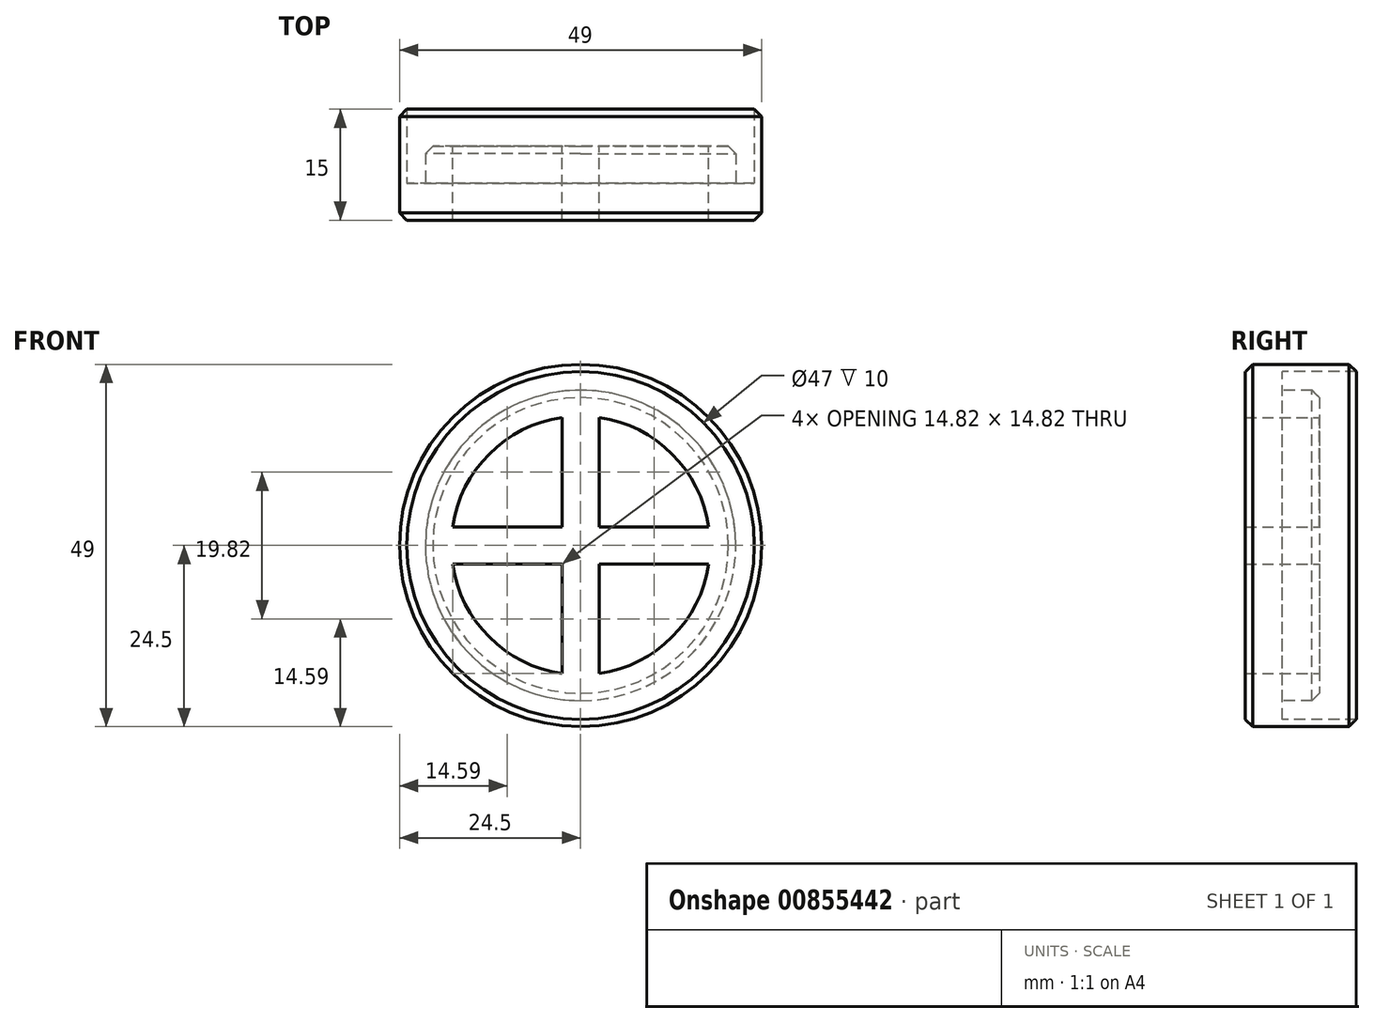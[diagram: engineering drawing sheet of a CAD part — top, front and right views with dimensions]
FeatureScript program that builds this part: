
annotation { "Feature Type Name" : "Feature", "Feature Type Description" : "" }
export const myFeature = defineFeature(function(context is Context, id is Id, definition is map)
    precondition{}
    {
        {
            var Q0;
            Q0=qCreatedBy(makeId("Top.planeOp"),FACE);
            var sketch = newSketch(context, id + "F0", { "sketchPlane" : qUnion([Q0])});
            skLineSegment(sketch, "E0", {"start": v(-24.5, 0) * mm, "end": v(0, 0) * mm});
            skLineSegment(sketch, "E1", {"start": v(-21, 10) * mm, "end": v(0, 10) * mm});
            skLineSegment(sketch, "E2", {"start": v(-24.5, 0) * mm, "end": v(-24.5, 15) * mm});
            skLineSegment(sketch, "E3", {"start": v(-24.5, 15) * mm, "end": v(-23.5, 15) * mm});
            skLineSegment(sketch, "E4", {"start": v(-23.5, 15) * mm, "end": v(-23.5, 5) * mm});
            skLineSegment(sketch, "E5", {"start": v(-23.5, 5) * mm, "end": v(-21, 5) * mm});
            skLineSegment(sketch, "E6", {"start": v(-21, 5) * mm, "end": v(-21, 10) * mm});
            skLineSegment(sketch, "E7", {"start": v(24.5, 15) * mm, "end": v(23.5, 15) * mm});
            skLineSegment(sketch, "E8", {"start": v(0, -24.54) * mm, "end": v(0, 28.01) * mm});
            skPoint(sketch, "E9.end.orphan", {"position": v(21, 5) * mm});
            skPoint(sketch, "E10.end.orphan", {"position": v(23.5, 5) * mm});
            skPoint(sketch, "E11.start.orphan", {"position": v(24.5, 0) * mm});
            skSolve(sketch);
        }
        {
            var Q0;
            Q0 = qSketchRegion(id + "F0", true);
            var Q1;
            Q1=sQuery(id+"F0.wireOp",EDGE,"E8");
            revolve(context, id + "F1", {"surfaceOperationType" : NewSurfaceOperationType.NEW, "entities" : qUnion([Q0]), "axis" : qUnion([Q1]), "revolveType" : RevolveType.FULL});
        }
        {
            var Q0;
            Q0=makeQuery(id+"F1.opRevolve","SWEPT_FACE",FACE,{"disambiguationData":[OSD([sQuery(id+"F0.wireOp",EDGE,"E1")])]});
            var sketch = newSketch(context, id + "F2", { "sketchPlane" : qUnion([Q0])});
            skArc(sketch, "E12", {"start": v(-17.32, -2.5) * mm, "mid": v(-12.37, -12.37) * mm, "end": v(-2.5, -17.32) * mm});
            skLineSegment(sketch, "E13", {"start": v(2.5, 17.32) * mm, "end": v(2.5, 2.5) * mm});
            skLineSegment(sketch, "E14", {"start": v(-2.5, 17.32) * mm, "end": v(-2.5, 2.5) * mm});
            skLineSegment(sketch, "E15", {"start": v(-17.32, -2.5) * mm, "end": v(-2.5, -2.5) * mm});
            skLineSegment(sketch, "E16", {"start": v(-17.32, 2.5) * mm, "end": v(-2.5, 2.5) * mm});
            skLineSegment(sketch, "E17.trimOffspring", {"start": v(2.5, 2.5) * mm, "end": v(17.32, 2.5) * mm});
            skLineSegment(sketch, "E18.trimOffspring", {"start": v(2.5, -2.5) * mm, "end": v(17.32, -2.5) * mm});
            skArc(sketch, "E19.trimOffspring", {"start": v(17.32, 2.5) * mm, "mid": v(12.37, 12.37) * mm, "end": v(2.5, 17.32) * mm});
            skArc(sketch, "E20.trimOffspring", {"start": v(-2.5, 17.32) * mm, "mid": v(-12.37, 12.37) * mm, "end": v(-17.32, 2.5) * mm});
            skLineSegment(sketch, "E21.trimOffspring", {"start": v(2.5, -2.5) * mm, "end": v(2.5, -17.32) * mm});
            skLineSegment(sketch, "E22.trimOffspring", {"start": v(-2.5, -2.5) * mm, "end": v(-2.5, -17.32) * mm});
            skArc(sketch, "E23.trimOffspring", {"start": v(2.5, -17.32) * mm, "mid": v(12.37, -12.37) * mm, "end": v(17.32, -2.5) * mm});
            skSolve(sketch);
        }
        {
            var Q0;
            Q0 = qSketchRegion(id + "F2", true);
            extrude(context, id + "F3", {"entities" : qUnion([Q0]), "operationType" : NewBodyOperationType.REMOVE, "oppositeDirection" : true, "depth" : 25 * mm, "offsetDistance" : 25 * mm});
        }
        {
            var Q0;
            Q0=makeQuery(id+"F1.opRevolve","SWEPT_EDGE",EDGE,{"disambiguationData":[OSD([sQuery(id+"F0.wireOp",EDGE,"E0"),sQuery(id+"F0.wireOp",EDGE,"E2")])]});
            var Q1;
            Q1=makeQuery(id+"F1.opRevolve","SWEPT_EDGE",EDGE,{"disambiguationData":[OSD([sQuery(id+"F0.wireOp",EDGE,"E2"),sQuery(id+"F0.wireOp",EDGE,"E3")])]});
            var Q2;
            Q2=makeQuery(id+"F1.opRevolve","SWEPT_EDGE",EDGE,{"disambiguationData":[OSD([sQuery(id+"F0.wireOp",EDGE,"E1"),sQuery(id+"F0.wireOp",EDGE,"E6")])]});
            chamfer(context, id + "F4", {"entities" : qUnion([Q0, Q1, Q2]), "width" : 1 * mm, "tangentPropagation" : true});
        }
    });
